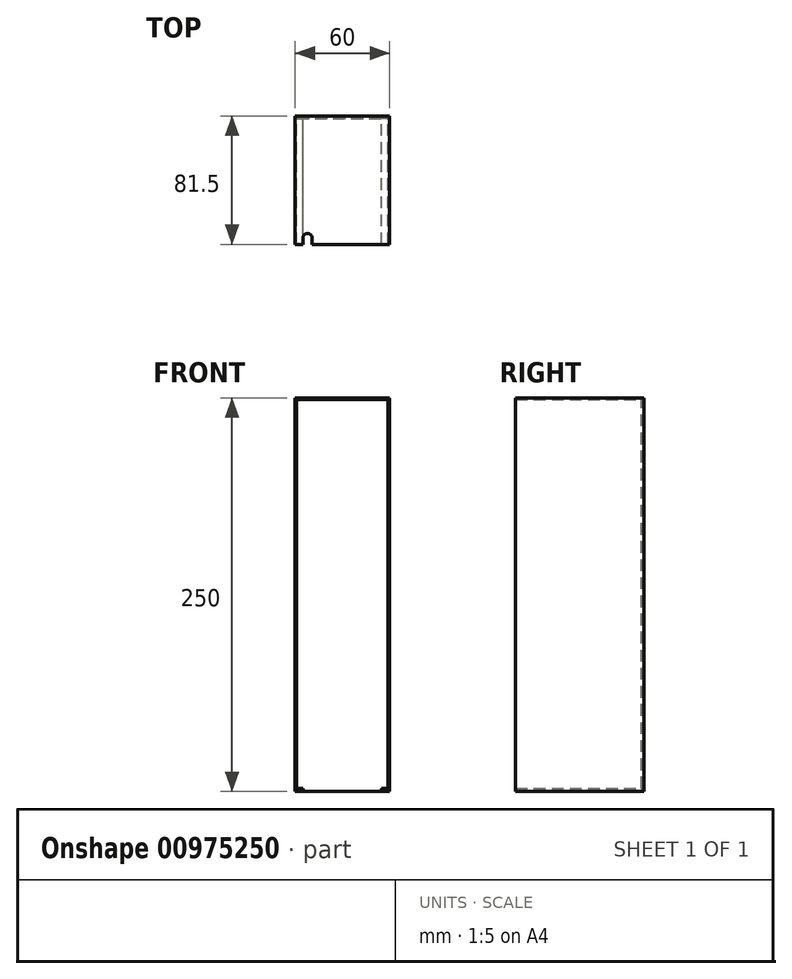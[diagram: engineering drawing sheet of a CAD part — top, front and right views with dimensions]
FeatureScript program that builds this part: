
annotation { "Feature Type Name" : "Feature", "Feature Type Description" : "" }
export const myFeature = defineFeature(function(context is Context, id is Id, definition is map)
    precondition{}
    {
        {
            var Q0;
            Q0=qCreatedBy(makeId("Front.planeOp"),FACE);
            var sketch = newSketch(context, id + "F0", { "sketchPlane" : qUnion([Q0])});
            skLineSegment(sketch, "E0", {"start": v(-30, 168.83) * mm, "end": v(30, 168.83) * mm});
            skLineSegment(sketch, "E1", {"start": v(30, 168.83) * mm, "end": v(30, -81.17) * mm});
            skLineSegment(sketch, "E2", {"start": v(30, -81.17) * mm, "end": v(-30, -81.17) * mm});
            skLineSegment(sketch, "E3", {"start": v(-30, -81.17) * mm, "end": v(-30, 168.83) * mm});
            skLineSegment(sketch, "E4", {"start": v(-29, 167.83) * mm, "end": v(29, 167.83) * mm});
            skLineSegment(sketch, "E5", {"start": v(29, 167.83) * mm, "end": v(29, -79.17) * mm});
            skLineSegment(sketch, "E6", {"start": v(29, -79.17) * mm, "end": v(25, -79.17) * mm});
            skLineSegment(sketch, "E7", {"start": v(-29, -79.17) * mm, "end": v(-29, 167.83) * mm});
            skLineSegment(sketch, "E8", {"start": v(-25, -79.17) * mm, "end": v(-25, -81.17) * mm});
            skLineSegment(sketch, "E9", {"start": v(25, -79.17) * mm, "end": v(25, -81.17) * mm});
            skLineSegment(sketch, "E10.trimOffspring", {"start": v(-25, -79.17) * mm, "end": v(-29, -79.17) * mm});
            skSolve(sketch);
        }
        {
            var Q0;
            Q0=makeQuery(id+"F0.imprint","IMPRINT",FACE,{"disambiguationData":[TD([[makeQuery(id+"F0.imprint","IMPRINT",EDGE,{"derivedFrom":sQuery(id+"F0.wireOp",EDGE,"E0")}),-1.0]])]});
            extrude(context, id + "F1", {"entities" : qUnion([Q0]), "depth" : 80 * mm, "offsetDistance" : 25 * mm});
        }
        {
            var Q0;
            Q0=makeQuery(id+"F1.opExtrude","CAP_FACE",FACE,{"disambiguationData":[OSD([sQuery(id+"F0.wireOp",EDGE,"E0"),sQuery(id+"F0.wireOp",EDGE,"E1"),sQuery(id+"F0.wireOp",EDGE,"E2"),sQuery(id+"F0.wireOp",EDGE,"E3"),sQuery(id+"F0.wireOp",EDGE,"E4"),sQuery(id+"F0.wireOp",EDGE,"E5"),sQuery(id+"F0.wireOp",EDGE,"E6"),sQuery(id+"F0.wireOp",EDGE,"E7"),sQuery(id+"F0.wireOp",EDGE,"E8"),sQuery(id+"F0.wireOp",EDGE,"E9"),sQuery(id+"F0.wireOp",EDGE,"E10.trimOffspring")])],"isStart":true});
            var sketch = newSketch(context, id + "F2", { "sketchPlane" : qUnion([Q0])});
            skLineSegment(sketch, "E11.bottom", {"start": v(-30, 168.83) * mm, "end": v(30, 168.83) * mm});
            skLineSegment(sketch, "E11.top", {"start": v(-30, -81.17) * mm, "end": v(30, -81.17) * mm});
            skLineSegment(sketch, "E11.left", {"start": v(-30, 168.83) * mm, "end": v(-30, -81.17) * mm});
            skLineSegment(sketch, "E11.right", {"start": v(30, 168.83) * mm, "end": v(30, -81.17) * mm});
            skSolve(sketch);
        }
        {
            var Q0;
            Q0 = qSketchRegion(id + "F2", true);
            extrude(context, id + "F3", {"entities" : qUnion([Q0]), "operationType" : NewBodyOperationType.ADD, "depth" : 1.5 * mm, "offsetDistance" : 25 * mm});
        }
        {
            var Q0;
            Q0=makeQuery(id+"F3.boolean.opBoolean","MERGE",FACE,{"derivedFrom":[makeQuery(id+"F1.opExtrude","SWEPT_FACE",FACE,{"disambiguationData":[OSD([sQuery(id+"F0.wireOp",EDGE,"E0")])]}),makeQuery(id+"F3.opExtrude","SWEPT_FACE",FACE,{"disambiguationData":[OSD([sQuery(id+"F2.wireOp",EDGE,"E11.bottom")])]})]});
            var sketch = newSketch(context, id + "F4", { "sketchPlane" : qUnion([Q0])});
            skLineSegment(sketch, "E12", {"start": v(-4.15, -81.17) * mm, "end": v(-4.15, -80.17) * mm});
            skArc(sketch, "E13", {"start": v(-19.12, -76.21) * mm, "mid": v(-22.17, -73.12) * mm, "end": v(-25.12, -76.31) * mm});
            skLineSegment(sketch, "E14", {"start": v(-25.12, -76.31) * mm, "end": v(-25.12, -80) * mm});
            skLineSegment(sketch, "E15", {"start": v(-19.12, -80) * mm, "end": v(-19.12, -76.21) * mm});
            skSolve(sketch);
        }
        {
            var Q0;
            Q0=makeQuery(id+"F4.imprint","IMPRINT",FACE,{"disambiguationData":[TD([[makeQuery(id+"F4.imprint","IMPRINT",EDGE,{"derivedFrom":sQuery(id+"F4.wireOp",EDGE,"E13")}),1.0]])]});
            extrude(context, id + "F5", {"entities" : qUnion([Q0]), "operationType" : NewBodyOperationType.REMOVE, "oppositeDirection" : true, "depth" : 1 * mm, "offsetDistance" : 25 * mm});
        }
    });
